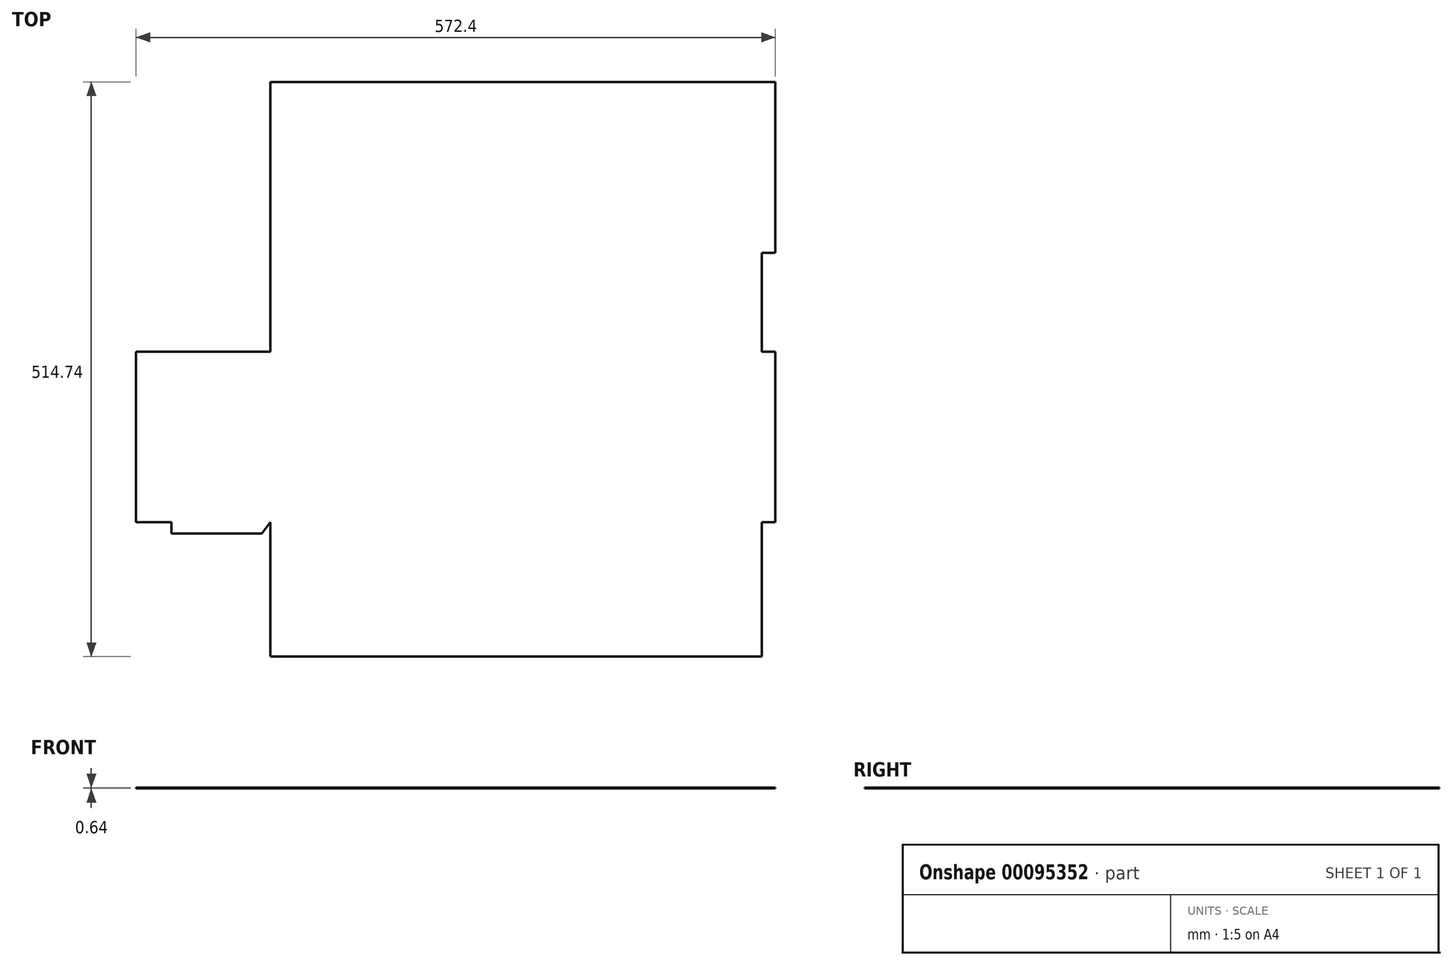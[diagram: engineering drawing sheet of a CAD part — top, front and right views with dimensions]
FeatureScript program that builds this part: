
annotation { "Feature Type Name" : "Feature", "Feature Type Description" : "" }
export const myFeature = defineFeature(function(context is Context, id is Id, definition is map)
    precondition{}
    {
        {
            var Q0;
            Q0=qCreatedBy(makeId("Top.planeOp"),FACE);
            var sketch = newSketch(context, id + "F0", { "sketchPlane" : qUnion([Q0])});
            skLineSegment(sketch, "E0.bottom", {"start": v(0, 0) * mm, "end": v(440, 0) * mm});
            skLineSegment(sketch, "E0.top", {"start": v(0, -88.7) * mm, "end": v(440, -88.7) * mm});
            skLineSegment(sketch, "E0.left", {"start": v(0, 0) * mm, "end": v(0, -88.7) * mm});
            skLineSegment(sketch, "E0.right", {"start": v(440, 0) * mm, "end": v(440, -88.7) * mm});
            skLineSegment(sketch, "E1.top", {"start": v(0, 152.87) * mm, "end": v(440, 152.87) * mm});
            skLineSegment(sketch, "E1.left", {"start": v(0, 0) * mm, "end": v(0, 152.87) * mm});
            skLineSegment(sketch, "E1.right", {"start": v(440, 0) * mm, "end": v(440, 152.87) * mm});
            skLineSegment(sketch, "E2.top", {"start": v(0, -241.57) * mm, "end": v(440, -241.57) * mm});
            skLineSegment(sketch, "E2.left", {"start": v(0, -88.7) * mm, "end": v(0, -241.57) * mm});
            skLineSegment(sketch, "E2.right", {"start": v(440, -88.7) * mm, "end": v(440, -241.57) * mm});
            skLineSegment(sketch, "E3.bottom", {"start": v(0, -88.7) * mm, "end": v(-88.7, -88.7) * mm});
            skLineSegment(sketch, "E3.top", {"start": v(0, -241.57) * mm, "end": v(-88.7, -241.57) * mm});
            skLineSegment(sketch, "E3.right", {"start": v(-88.7, -88.7) * mm, "end": v(-88.7, -241.57) * mm});
            skLineSegment(sketch, "E4.top", {"start": v(0, -330.27) * mm, "end": v(440, -330.27) * mm});
            skLineSegment(sketch, "E4.left", {"start": v(0, -241.57) * mm, "end": v(0, -330.27) * mm});
            skLineSegment(sketch, "E4.right", {"start": v(440, -241.57) * mm, "end": v(440, -330.27) * mm});
            skLineSegment(sketch, "E5.top", {"start": v(0, -361.87) * mm, "end": v(440, -361.87) * mm});
            skLineSegment(sketch, "E5.left", {"start": v(0, -330.27) * mm, "end": v(0, -361.87) * mm});
            skLineSegment(sketch, "E5.right", {"start": v(440, -330.27) * mm, "end": v(440, -361.87) * mm});
            skLineSegment(sketch, "E6.bottom", {"start": v(-88.7, -88.7) * mm, "end": v(0, -88.7) * mm});
            skLineSegment(sketch, "E7.bottom", {"start": v(-88.7, -88.7) * mm, "end": v(-120.3, -88.7) * mm});
            skLineSegment(sketch, "E7.top", {"start": v(-88.7, -241.57) * mm, "end": v(-120.3, -241.57) * mm});
            skLineSegment(sketch, "E7.right", {"start": v(-120.3, -88.7) * mm, "end": v(-120.3, -241.57) * mm});
            skLineSegment(sketch, "E8.bottom", {"start": v(440, -88.7) * mm, "end": v(452.1, -88.7) * mm});
            skLineSegment(sketch, "E8.top", {"start": v(440, -241.57) * mm, "end": v(452.1, -241.57) * mm});
            skLineSegment(sketch, "E8.right", {"start": v(452.1, -88.7) * mm, "end": v(452.1, -241.57) * mm});
            skLineSegment(sketch, "E9.bottom", {"start": v(440, 152.87) * mm, "end": v(452.1, 152.87) * mm});
            skLineSegment(sketch, "E9.top", {"start": v(440, 0) * mm, "end": v(452.1, 0) * mm});
            skLineSegment(sketch, "E9.left", {"start": v(440, 152.87) * mm, "end": v(440, 0) * mm});
            skLineSegment(sketch, "E9.right", {"start": v(452.1, 152.87) * mm, "end": v(452.1, 0) * mm});
            skLineSegment(sketch, "E10", {"start": v(-88.7, -88.7) * mm, "end": v(-88.7, -78.7) * mm});
            skLineSegment(sketch, "E11", {"start": v(-88.7, -78.7) * mm, "end": v(-7.79, -78.7) * mm});
            skLineSegment(sketch, "E12", {"start": v(-7.79, -78.7) * mm, "end": v(0, -88.7) * mm});
            skLineSegment(sketch, "E13", {"start": v(-88.7, -241.57) * mm, "end": v(-88.7, -251.57) * mm});
            skLineSegment(sketch, "E14", {"start": v(-88.7, -251.57) * mm, "end": v(-7.79, -251.57) * mm});
            skLineSegment(sketch, "E15", {"start": v(-7.79, -251.57) * mm, "end": v(0, -241.57) * mm});
            skSolve(sketch);
        }
        {
            var Q0;
            Q0=makeQuery(id+"F0.imprint","IMPRINT",FACE,{"disambiguationData":[TD([[makeQuery(id+"F0.imprint","IMPRINT",EDGE,{"derivedFrom":sQuery(id+"F0.wireOp",EDGE,"E0.bottom")}),1.0]])]});
            var Q1;
            Q1=makeQuery(id+"F0.imprint","IMPRINT",FACE,{"disambiguationData":[TD([[makeQuery(id+"F0.imprint","IMPRINT",EDGE,{"derivedFrom":sQuery(id+"F0.wireOp",EDGE,"E0.left")}),1.0]])]});
            var Q2;
            Q2=makeQuery(id+"F0.imprint","IMPRINT",FACE,{"disambiguationData":[TD([[makeQuery(id+"F0.imprint","IMPRINT",EDGE,{"derivedFrom":sQuery(id+"F0.wireOp",EDGE,"E9.bottom")}),-1.0]])]});
            var Q3;
            Q3=makeQuery(id+"F0.imprint","IMPRINT",FACE,{"disambiguationData":[TD([[makeQuery(id+"F0.imprint","IMPRINT",EDGE,{"derivedFrom":sQuery(id+"F0.wireOp",EDGE,"E0.top")}),-1.0]])]});
            var Q4;
            Q4=makeQuery(id+"F0.imprint","IMPRINT",FACE,{"disambiguationData":[TD([[makeQuery(id+"F0.imprint","IMPRINT",EDGE,{"derivedFrom":sQuery(id+"F0.wireOp",EDGE,"E8.bottom")}),-1.0]])]});
            var Q5;
            Q5=makeQuery(id+"F0.imprint","IMPRINT",FACE,{"disambiguationData":[TD([[makeQuery(id+"F0.imprint","IMPRINT",EDGE,{"derivedFrom":sQuery(id+"F0.wireOp",EDGE,"E2.top")}),-1.0]])]});
            var Q6;
            Q6=makeQuery(id+"F0.imprint","IMPRINT",FACE,{"disambiguationData":[TD([[makeQuery(id+"F0.imprint","IMPRINT",EDGE,{"derivedFrom":sQuery(id+"F0.wireOp",EDGE,"E4.top")}),-1.0]])]});
            var Q7;
            Q7=makeQuery(id+"F0.imprint","IMPRINT",FACE,{"disambiguationData":[TD([[makeQuery(id+"F0.imprint","IMPRINT",EDGE,{"derivedFrom":sQuery(id+"F0.wireOp",EDGE,"E3.top")}),-1.0]])]});
            var Q8;
            Q8=makeQuery(id+"F0.imprint","IMPRINT",FACE,{"disambiguationData":[TD([[makeQuery(id+"F0.imprint","IMPRINT",EDGE,{"derivedFrom":sQuery(id+"F0.wireOp",EDGE,"E7.bottom")}),1.0]])]});
            var Q9;
            Q9=makeQuery(id+"F0.imprint","IMPRINT",FACE,{"disambiguationData":[TD([[makeQuery(id+"F0.imprint","IMPRINT",EDGE,{"derivedFrom":sQuery(id+"F0.wireOp",EDGE,"E6.bottom")}),1.0]])]});
            var Q10;
            Q10=makeQuery(id+"F0.imprint","IMPRINT",FACE,{"disambiguationData":[TD([[makeQuery(id+"F0.imprint","IMPRINT",EDGE,{"derivedFrom":sQuery(id+"F0.wireOp",EDGE,"E3.top")}),1.0]])]});
            extrude(context, id + "F1", {"entities" : qUnion([Q0, Q1, Q2, Q3, Q4, Q5, Q6, Q7, Q8, Q9, Q10]), "depth" : 0.64 * mm});
        }
    });
